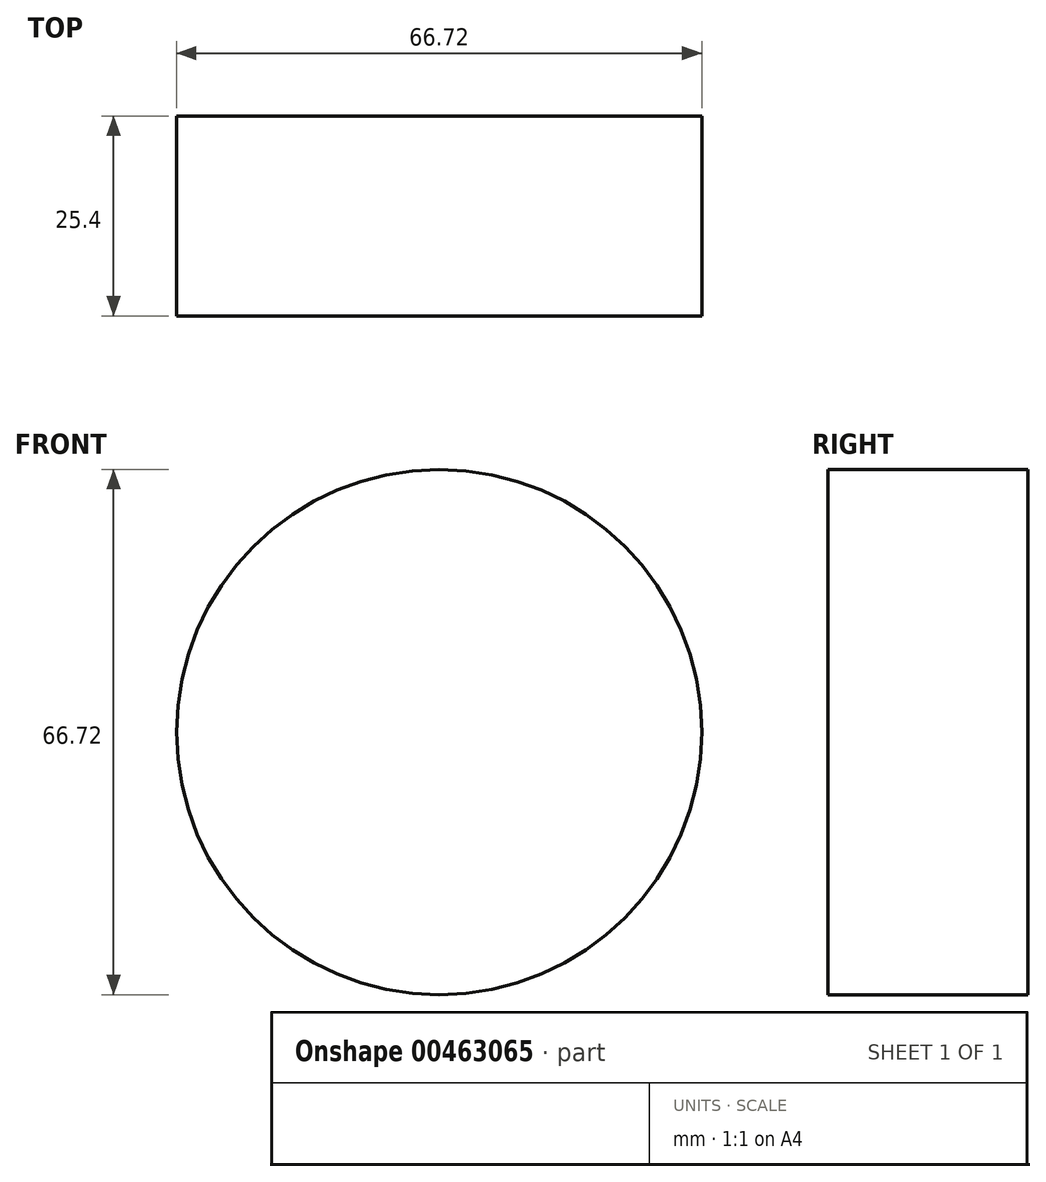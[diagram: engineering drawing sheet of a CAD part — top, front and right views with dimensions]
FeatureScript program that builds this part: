
annotation { "Feature Type Name" : "Feature", "Feature Type Description" : "" }
export const myFeature = defineFeature(function(context is Context, id is Id, definition is map)
    precondition{}
    {
        {
            var Q0;
            Q0=qCreatedBy(makeId("Front.planeOp"),FACE);
            var sketch = newSketch(context, id + "F0", { "sketchPlane" : qUnion([Q0])});
            skCircle(sketch, "E0", {"center": v(0, 0) * mm, "radius": 33.36 * mm});
            skSolve(sketch);
        }
        {
            var Q0;
            Q0 = qSketchRegion(id + "F0", true);
            extrude(context, id + "F1", {"entities" : qUnion([Q0]), "depth" : 25.4 * mm});
        }
    });
